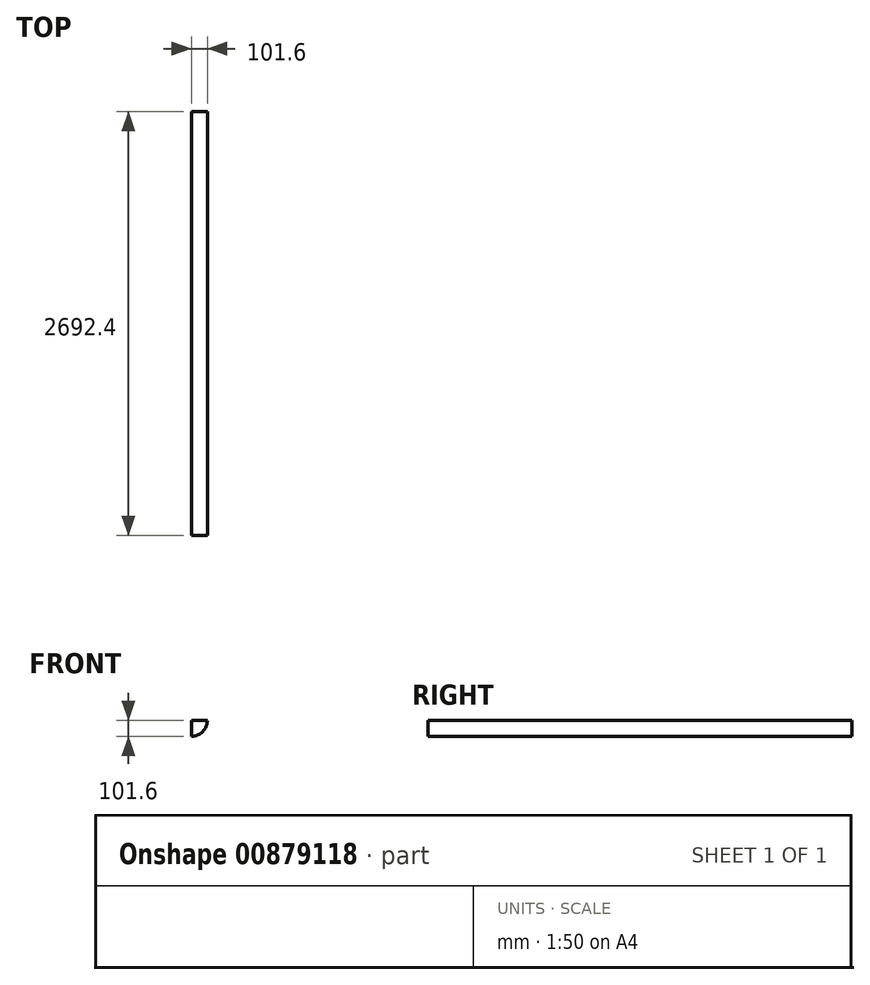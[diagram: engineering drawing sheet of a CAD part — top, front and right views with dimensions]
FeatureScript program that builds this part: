
annotation { "Feature Type Name" : "Feature", "Feature Type Description" : "" }
export const myFeature = defineFeature(function(context is Context, id is Id, definition is map)
    precondition{}
    {
        {
            var Q0;
            Q0=qCreatedBy(makeId("Front.planeOp"),FACE);
            var sketch = newSketch(context, id + "F0", { "sketchPlane" : qUnion([Q0])});
            skArc(sketch, "E0", {"start": v(0, -101.6) * mm, "mid": v(71.84, -71.84) * mm, "end": v(101.6, 0) * mm});
            skLineSegment(sketch, "E1", {"start": v(0, 0) * mm, "end": v(101.6, 0) * mm});
            skLineSegment(sketch, "E2", {"start": v(0, 0) * mm, "end": v(0, -101.6) * mm});
            skSolve(sketch);
        }
        {
            var Q0;
            Q0=qSketchRegion(id+"F0",true);
            extrude(context, id + "F1", {"entities" : qUnion([Q0]), "depth" : 2692.4 * mm, "offsetDistance" : 25.4 * mm});
        }
    });
